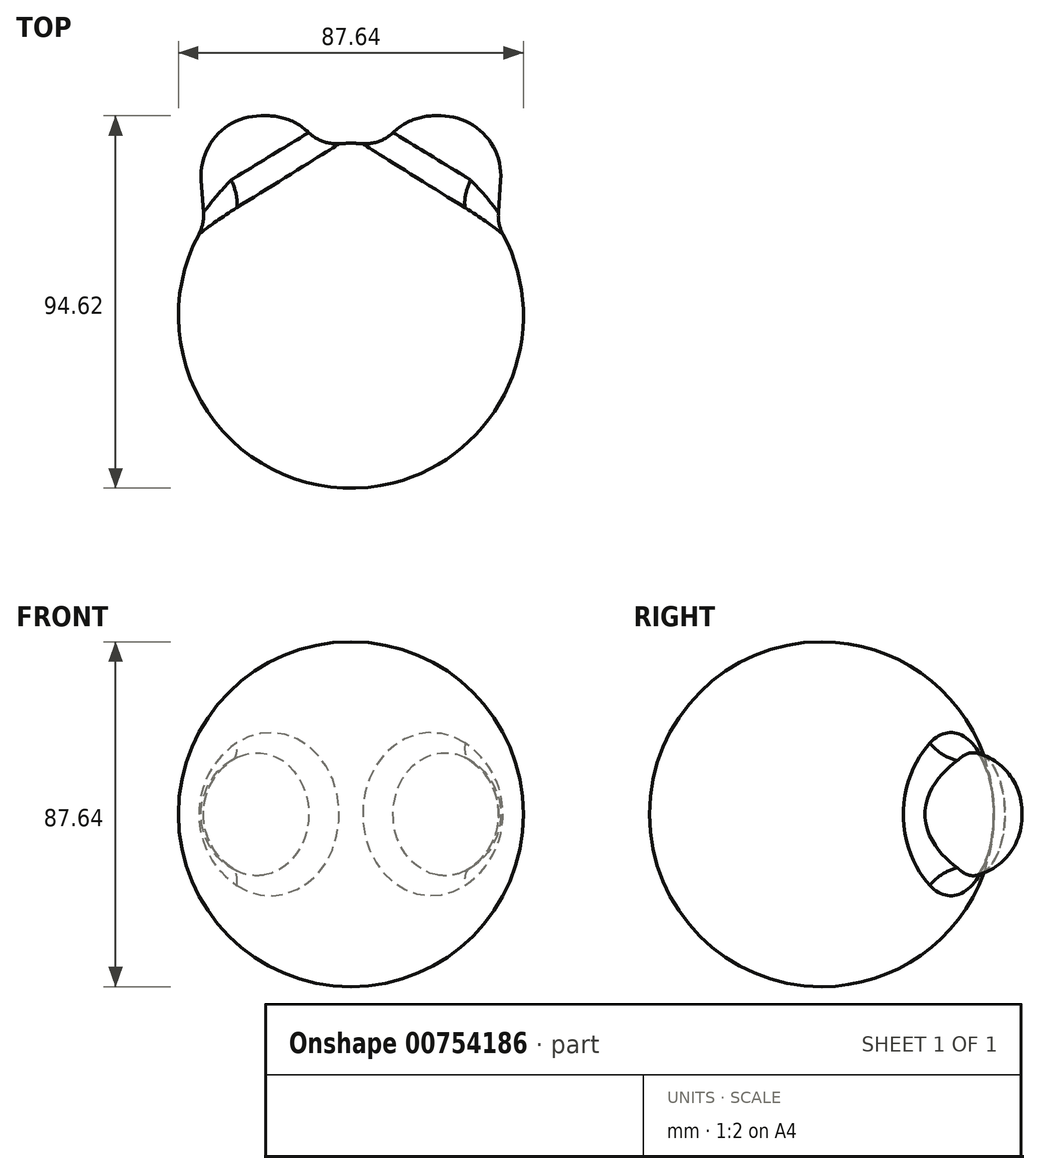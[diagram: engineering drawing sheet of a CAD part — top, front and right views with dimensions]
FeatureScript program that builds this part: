
annotation { "Feature Type Name" : "Feature", "Feature Type Description" : "" }
export const myFeature = defineFeature(function(context is Context, id is Id, definition is map)
    precondition{}
    {
        {
            var Q0;
            Q0=qCreatedBy(makeId("Front.planeOp"),FACE);
            var sketch = newSketch(context, id + "F0", { "sketchPlane" : qUnion([Q0])});
            skArc(sketch, "E0", {"start": v(0, 43.82) * mm, "mid": v(-43.82, 0) * mm, "end": v(0, -43.82) * mm});
            skLineSegment(sketch, "E1", {"start": v(0, 43.82) * mm, "end": v(0, -43.82) * mm});
            skSolve(sketch);
        }
        {
            var Q0;
            Q0 = qSketchRegion(id + "F0", true);
            var Q1;
            Q1=sQuery(id+"F0.wireOp",EDGE,"E1");
            revolve(context, id + "F1", {"surfaceOperationType" : NewSurfaceOperationType.NEW, "entities" : qUnion([Q0]), "axis" : qUnion([Q1]), "revolveType" : RevolveType.FULL});
        }
        {
            var Q0;
            Q0=qCreatedBy(makeId("Front.planeOp"),FACE);
            var sketch = newSketch(context, id + "F2", { "sketchPlane" : qUnion([Q0])});
            skCircle(sketch, "E2", {"center": v(22.06, 0) * mm, "radius": 13.57 * mm});
            skCircle(sketch, "E3.MirrorC", {"center": v(-22.06, 0) * mm, "radius": 13.57 * mm});
            skSolve(sketch);
        }
        {
            var Q0;
            Q0 = qSketchRegion(id + "F2", true);
            extrude(context, id + "F3", {"entities" : qUnion([Q0]), "operationType" : NewBodyOperationType.ADD, "oppositeDirection" : true, "depth" : 50.8 * mm, "offsetDistance" : 25.4 * mm, "hasDraft" : true, "draftAngle" : 4 * degree});
        }
        {
            var Q0;
            Q0=makeQuery(id+"F3.opExtrude","CAP_EDGE",EDGE,{"disambiguationData":[OSD([sQuery(id+"F2.wireOp",EDGE,"E2")])],"isStart":false});
            var Q1;
            Q1=makeQuery(id+"F3.opExtrude","CAP_EDGE",EDGE,{"disambiguationData":[OSD([sQuery(id+"F2.wireOp",EDGE,"E3.MirrorC")])],"isStart":false});
            fillet(context, id + "F4", {"entities" : qUnion([Q0, Q1]), "radius" : 15.24 * mm, "tangentPropagation" : true, "allowEdgeOverflow" : false});
        }
        {
            var Q0;
            Q0=makeQuery(id+"F3.boolean.opBoolean","INTERSECT",EDGE,{"derivedFrom":[makeQuery(id+"F1.opRevolve","SWEPT_FACE",FACE,{"disambiguationData":[OSD([sQuery(id+"F0.wireOp",EDGE,"E0")])]}),makeQuery(id+"F3.opExtrude","SWEPT_FACE",FACE,{"disambiguationData":[OSD([sQuery(id+"F2.wireOp",EDGE,"E2")])]})]});
            var Q1;
            Q1=makeQuery(id+"F3.boolean.opBoolean","INTERSECT",EDGE,{"derivedFrom":[makeQuery(id+"F1.opRevolve","SWEPT_FACE",FACE,{"disambiguationData":[OSD([sQuery(id+"F0.wireOp",EDGE,"E0")])]}),makeQuery(id+"F3.opExtrude","SWEPT_FACE",FACE,{"disambiguationData":[OSD([sQuery(id+"F2.wireOp",EDGE,"E3.MirrorC")])]})]});
            fillet(context, id + "F5", {"entities" : qUnion([Q0, Q1]), "radius" : 10.16 * mm, "tangentPropagation" : true, "allowEdgeOverflow" : false});
        }
    });
